# Revit family: DIN-Kreuzverbinder für Flachleiter VA-V4A
name_source: partatom
category: Generic Models
revit_build: Autodesk Revit 2015 (Build: 20140606_1530(x64)
units: mm (PartAtom-declared; Revit-internal decimal feet)

## types (2) — shared parameters
Height = 3 mm  [stored 0.00984252 ft]
Height 1 = 2 mm  [stored 0.00656168 ft]
Length = 60 mm  [stored 0.19685 ft]
Length 1 = 20 mm  [stored 0.0656168 ft]
Length 2 = 14 mm  [stored 0.0459318 ft]
Manufacturer = OBO Bettermann
Material = Stainless Steel
URL = http://www.obo-bettermann.com
Width = 60 mm  [stored 0.19685 ft]
Width 1 = 20 mm  [stored 0.0656168 ft]
Width 2 = 13 mm

## per-type parameters (varying)
| type | GTIN | Manufacturer Art.No. |
| 256 A-DIN 30 VA | 4012195925873 | 5314720 |
| 256 A-DIN 30 V4A | 4012195893080 | 5314659 |

note: column(s) folded — value = type name in every type: Article Type

note: [stored X ft] marks values corroborated as IEEE doubles in the binary element streams (Revit-internal decimal feet)

## geometry (parser evidence)
native form markers: Sweep x2
no freeform markers — native parametric forms only
